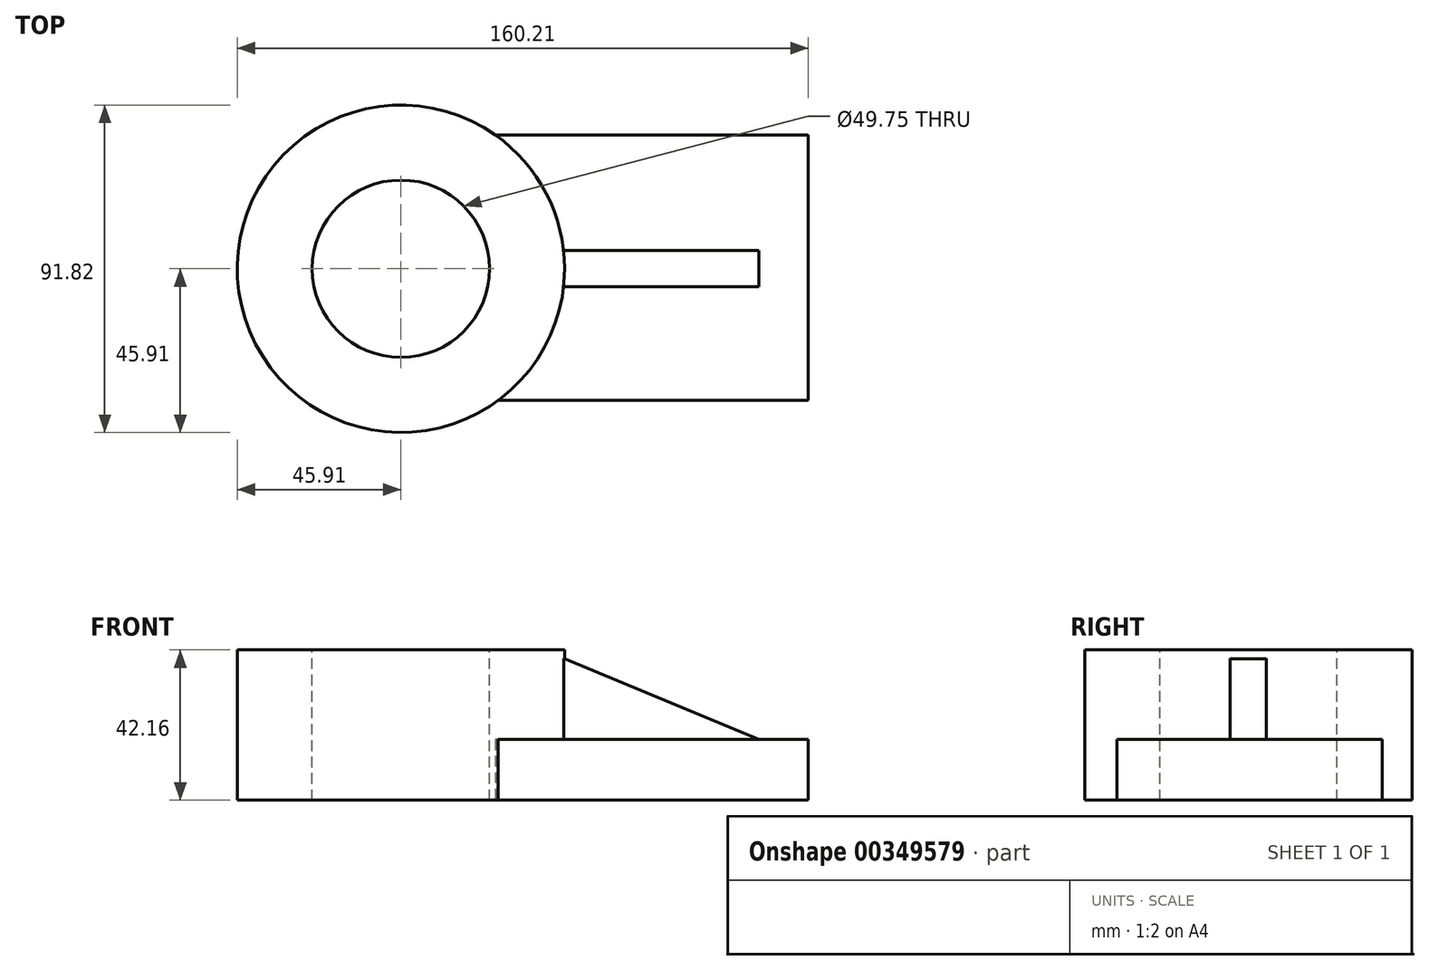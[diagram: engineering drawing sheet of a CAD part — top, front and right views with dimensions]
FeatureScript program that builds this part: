
annotation { "Feature Type Name" : "Feature", "Feature Type Description" : "" }
export const myFeature = defineFeature(function(context is Context, id is Id, definition is map)
    precondition{}
    {
        {
            var Q0;
            Q0=qCreatedBy(makeId("Top.planeOp"),FACE);
            var sketch = newSketch(context, id + "F0", { "sketchPlane" : qUnion([Q0])});
            skCircle(sketch, "E0", {"center": v(0, 0) * mm, "radius": 45.91 * mm});
            skSolve(sketch);
        }
        {
            var Q0;
            Q0 = qSketchRegion(id + "F0", true);
            extrude(context, id + "F1", {"entities" : qUnion([Q0]), "depth" : 42.16 * mm});
        }
        {
            var Q0;
            Q0=qCreatedBy(makeId("Right.planeOp"),FACE);
            var sketch = newSketch(context, id + "F2", { "sketchPlane" : qUnion([Q0])});
            skLineSegment(sketch, "E1", {"start": v(-45.91, 0) * mm, "end": v(-45.91, 42.16) * mm});
            skLineSegment(sketch, "E2", {"start": v(45.91, 42.16) * mm, "end": v(45.91, 0) * mm});
            skLineSegment(sketch, "E3.bottom", {"start": v(-36.95, 0) * mm, "end": v(37.48, 0) * mm});
            skLineSegment(sketch, "E3.top", {"start": v(-36.95, 17.01) * mm, "end": v(37.48, 17.01) * mm});
            skLineSegment(sketch, "E3.left", {"start": v(-36.95, 0) * mm, "end": v(-36.95, 17.01) * mm});
            skLineSegment(sketch, "E3.right", {"start": v(37.48, 0) * mm, "end": v(37.48, 17.01) * mm});
            skSolve(sketch);
        }
        {
            var Q0;
            Q0 = qSketchRegion(id + "F2", true);
            extrude(context, id + "F3", {"entities" : qUnion([Q0]), "operationType" : NewBodyOperationType.ADD, "depth" : 114.3 * mm});
        }
        {
            var Q0;
            Q0=qCreatedBy(makeId("Front.planeOp"),FACE);
            var sketch = newSketch(context, id + "F4", { "sketchPlane" : qUnion([Q0])});
            skLineSegment(sketch, "E4.0", {"start": v(114.3, 17.01) * mm, "end": v(26.52, 17.01) * mm});
            skLineSegment(sketch, "E5", {"start": v(100.39, 17.01) * mm, "end": v(42.7, 17.01) * mm});
            skLineSegment(sketch, "E6", {"start": v(42.7, 17.01) * mm, "end": v(42.7, 40.94) * mm});
            skLineSegment(sketch, "E7", {"start": v(42.7, 40.94) * mm, "end": v(100.39, 17.01) * mm});
            skSolve(sketch);
        }
        {
            var Q0;
            Q0 = qSketchRegion(id + "F4", true);
            extrude(context, id + "F5", {"entities" : qUnion([Q0]), "operationType" : NewBodyOperationType.ADD, "depth" : 5.08 * mm, "hasSecondDirection" : true, "secondDirectionOppositeDirection" : true, "secondDirectionDepth" : 5.08 * mm});
        }
        {
            var Q0;
            Q0=makeQuery(id+"F1.opExtrude","CAP_FACE",FACE,{"disambiguationData":[OSD([sQuery(id+"F0.wireOp",EDGE,"E0")])],"isStart":false});
            var sketch = newSketch(context, id + "F6", { "sketchPlane" : qUnion([Q0])});
            skCircle(sketch, "E8.0.0", {"center": v(0, 0) * mm, "radius": 45.91 * mm});
            skCircle(sketch, "E9", {"center": v(0, 0) * mm, "radius": 24.87 * mm});
            skSolve(sketch);
        }
        {
            var Q0;
            Q0=makeQuery(id+"F6.imprint","IMPRINT",FACE,{"disambiguationData":[TD([[makeQuery(id+"F6.imprint","IMPRINT",EDGE,{"derivedFrom":sQuery(id+"F6.wireOp",EDGE,"E9")}),1.0]])]});
            extrude(context, id + "F7", {"entities" : qUnion([Q0]), "operationType" : NewBodyOperationType.REMOVE, "endBound" : BoundingType.THROUGH_ALL, "oppositeDirection" : true, "depth" : 25.4 * mm});
        }
    });
